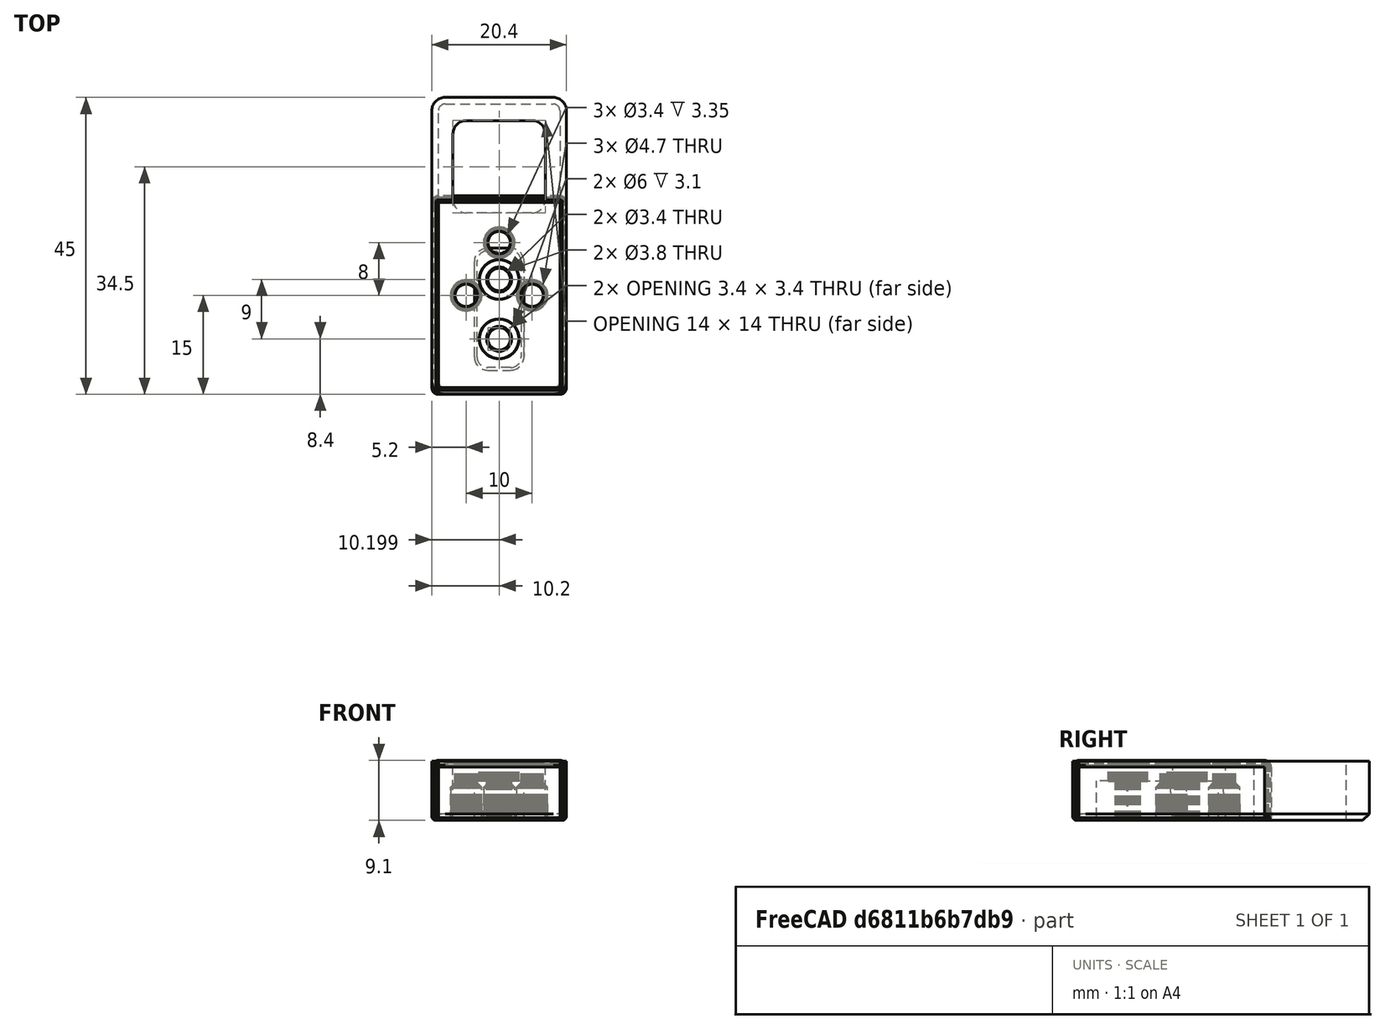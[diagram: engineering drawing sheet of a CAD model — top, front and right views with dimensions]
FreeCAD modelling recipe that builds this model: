
FCSTD DOCUMENT  (FreeCAD 0.19R24291 (Git))
Label: chain-back-supporter
License: Other
LicenseURL: GPL3
objects: Part::Cylinder×12, Part::MultiFuse×4, Part::Box×3, Part::Chamfer×3, Part::Cut×3, Part::Fillet×3, Part::Feature×1, Part::Refine×1
note: 30 computed .brp shape members not serialized (recipe doc carries the construction recipe); baked Part::Feature solids carry a one-line shape summary decoded from their .brp

FEATURE [Part::Feature] Z_Chain_3_Hole_Upper_Mount001_solid  label="Z_Chain_3_Hole_Upper_Mount001 (Solid)"
  shape: bbox 20.4 x 30.1 x 9.1 mm, 6608 faces (baked)
FEATURE [Part::Refine] Z_Chain_3_Hole_Upper_Mount001_solid001  label="Z_Chain_3_Hole_Upper_Mount001 (Solid)001"
  Placement = pos=(-11.2,0,0) rot=(0,0,1;0rad)
  Source = -> Z_Chain_3_Hole_Upper_Mount001_solid
FEATURE [Part::Box] Box  label="Cube"
  AttacherType = Attacher::AttachEngine3D
  Height = 9
  Length = 20.4
  Placement = pos=(-10.2,0,0) rot=(0,0,1;0rad)
  Width = 45
FEATURE [Part::Cylinder] Cylinder
  Angle = 360
  AttacherType = Attacher::AttachEngine3D
  Height = 10
  Placement = pos=(0,23,0) rot=(0,0,1;0rad)
  Radius = 1.7
FEATURE [Part::Cylinder] Cylinder001
  Angle = 360
  AttacherType = Attacher::AttachEngine3D
  Height = 10
  Placement = pos=(5,15,0) rot=(0,0,1;0rad)
  Radius = 1.7
FEATURE [Part::Cylinder] Cylinder002
  Angle = 360
  AttacherType = Attacher::AttachEngine3D
  Height = 10
  Placement = pos=(-5,15,0) rot=(0,0,1;0rad)
  Radius = 1.7
FEATURE [Part::Cylinder] Cylinder003
  Angle = 360
  AttacherType = Attacher::AttachEngine3D
  Height = 5.65
  Placement = pos=(-5,15,0) rot=(0,0,1;0rad)
  Radius = 2.35
FEATURE [Part::Cylinder] Cylinder004
  Angle = 360
  AttacherType = Attacher::AttachEngine3D
  Height = 5.65
  Placement = pos=(5,15,0) rot=(0,0,1;0rad)
  Radius = 2.35
FEATURE [Part::Cylinder] Cylinder005
  Angle = 360
  AttacherType = Attacher::AttachEngine3D
  Height = 5.65
  Placement = pos=(0,23,0) rot=(0,0,1;0rad)
  Radius = 2.35
FEATURE [Part::MultiFuse] Fusion
  Shapes = -> [Cylinder005,Cylinder004,Cylinder003,Cylinder002,Cylinder001,Cylinder]
FEATURE [Part::Chamfer] Chamfer001
  Base = -> Fusion
  Edges = 3 edges r=0.6: [Edge1,Edge8,Edge15]
FEATURE [Part::Cylinder] Cylinder006
  Angle = 360
  AttacherType = Attacher::AttachEngine3D
  Height = 10
  Placement = pos=(0,8.4,5.9) rot=(0,0,1;0rad)
  Radius = 3
FEATURE [Part::Cylinder] Cylinder007
  Angle = 360
  AttacherType = Attacher::AttachEngine3D
  Height = 10
  Placement = pos=(0,17.4,5.9) rot=(0,0,1;0rad)
  Radius = 3
FEATURE [Part::Cylinder] Cylinder008
  Angle = 360
  AttacherType = Attacher::AttachEngine3D
  Height = 10
  Placement = pos=(0,8.4,0) rot=(0,0,1;0rad)
  Radius = 1.7
FEATURE [Part::Cylinder] Cylinder009
  Angle = 360
  AttacherType = Attacher::AttachEngine3D
  Height = 10
  Placement = pos=(0,17.4,0) rot=(0,0,1;0rad)
  Radius = 1.7
FEATURE [Part::MultiFuse] Fusion001
  Shapes = -> [Cylinder009,Cylinder008,Cylinder007,Cylinder006]
FEATURE [Part::MultiFuse] Fusion002
  Shapes = -> [Chamfer001,Fusion001]
FEATURE [Part::Box] Box001  label="Cube001"
  AttacherType = Attacher::AttachEngine3D
  Height = 10
  Length = 14
  Placement = pos=(-7,27.5,0) rot=(0,0,1;0rad)
  Width = 14
FEATURE [Part::Cut] Cut
  Base = -> Box
  Tool = -> Box001
FEATURE [Part::Fillet] Fillet
  Base = -> Cut
  Edges = 4 edges r=2: [Edge21,Edge22,Edge23,Edge24]
FEATURE [Part::Fillet] Fillet001
  Base = -> Fillet
  Edges = 4 edges r=2: [Edge29,Edge30,Edge33,Edge35]
FEATURE [Part::Chamfer] Chamfer
  Base = -> Fillet001
  Edges = 8 edges r=1: [Edge18,Edge20,Edge22,Edge24,Edge26,Edge28,Edge30,Edge32]
FEATURE [Part::Cut] Cut001
  Base = -> Chamfer
  Tool = -> Fusion002
FEATURE [Part::Cylinder] Cylinder010
  Angle = 360
  AttacherType = Attacher::AttachEngine3D
  Height = 10
  Placement = pos=(0,8.4,0) rot=(0,0,1;0rad)
  Radius = 1.9
FEATURE [Part::Box] Box002  label="Cube002"
  AttacherType = Attacher::AttachEngine3D
  Height = 6
  Length = 7.5
  Placement = pos=(-3.75,3.65,0) rot=(0,0,1;0rad)
  Width = 18.5
FEATURE [Part::Cylinder] Cylinder011
  Angle = 360
  AttacherType = Attacher::AttachEngine3D
  Height = 10
  Placement = pos=(0,17.4,0) rot=(0,0,1;0rad)
  Radius = 1.9
FEATURE [Part::Fillet] Fillet002
  Base = -> Box002
  Edges = 4 edges r=2: [Edge1,Edge3,Edge5,Edge7]
FEATURE [Part::Chamfer] Chamfer002
  Base = -> Fillet002
  Edges = 8 edges r=0.4: [Edge3,Edge12,Edge14,Edge16,Edge17,Edge18,Edge19,Edge20]
FEATURE [Part::MultiFuse] Fusion003
  Shapes = -> [Cylinder011,Cylinder010]
FEATURE [Part::Cut] Cut002
  Base = -> Chamfer002
  Tool = -> Fusion003
